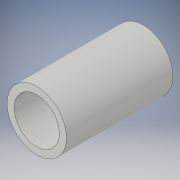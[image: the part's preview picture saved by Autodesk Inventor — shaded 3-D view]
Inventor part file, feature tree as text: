
AUTODESK INVENTOR PART (.ipt)
format: ipt  version: 2019 (Build 230136000, 136)  size: 97,280 bytes
history: native  units: in
note: dims shown in document units (in); Inventor stores cm internally (conversion verified against a paired STEP export)
features: extrude x1, sketch x1
ambient origin geometry x8: Origin, YZ Plane, XZ Plane, XY Plane, X Axis, Y Axis, Z Axis, Center Point
bodies: Solid1 (feature_tree)
feature tree (2):
  extrude  "Extrusion1"  Depth=2.985in
  sketch  "Sketch1"  dims[d0=1.265in d1=0.2in d2=2.985in d3=0.0in]
